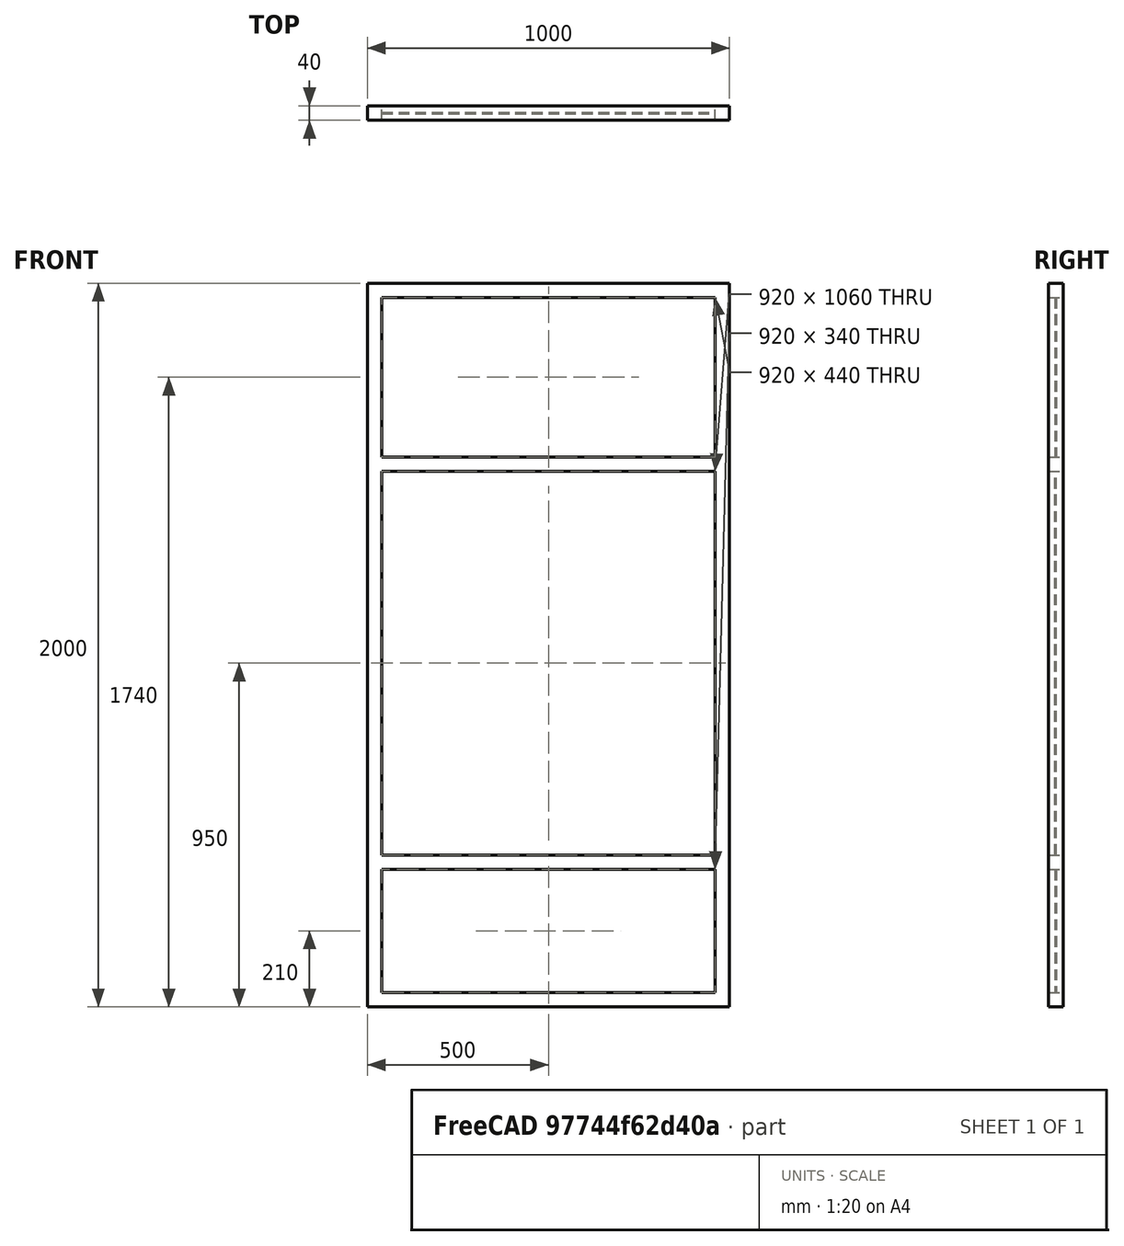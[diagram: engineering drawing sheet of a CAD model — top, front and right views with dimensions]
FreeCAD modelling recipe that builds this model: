
FCSTD DOCUMENT  (FreeCAD 0.16R6704 (Git))
Label: Window with 3 vertical fixed glass
License: CreativeCommons Attribution
LicenseURL: http://creativecommons.org/licenses/by/4.0/
objects: Sketcher::SketchObject×1, Part::FeaturePython×1
note: 2 computed .brp shape members not serialized (recipe doc carries the construction recipe); baked Part::Feature solids carry a one-line shape summary decoded from their .brp

FEATURE [Sketcher::SketchObject] Sketch114  label="Esboço caixilho fixo 3"
  Placement = pos=(0,0,0) rot=(1,0,0;1.5708rad)
  sketch-geometry (24):
    g0: LineSegment StartX=1000 StartY=2000 StartZ=0 EndX=0 EndY=2000 EndZ=0
    g1: LineSegment StartX=0 StartY=2000 StartZ=0 EndX=0 EndY=0 EndZ=0
    g2: LineSegment StartX=0 StartY=0 StartZ=0 EndX=1000 EndY=0 EndZ=0
    g3: LineSegment StartX=1000 StartY=0 StartZ=0 EndX=1000 EndY=2000 EndZ=0
    g4: LineSegment StartX=40 StartY=380 StartZ=0 EndX=960 EndY=380 EndZ=0
    g5: LineSegment StartX=960 StartY=380 StartZ=0 EndX=960 EndY=40 EndZ=0
    g6: LineSegment StartX=960 StartY=40 StartZ=0 EndX=40 EndY=40 EndZ=0
    g7: LineSegment StartX=40 StartY=40 StartZ=0 EndX=40 EndY=380 EndZ=0
    g8: LineSegment StartX=40 StartY=1960 StartZ=0 EndX=960 EndY=1960 EndZ=0
    g9: LineSegment StartX=960 StartY=1960 StartZ=0 EndX=960 EndY=1520 EndZ=0
    g10: LineSegment StartX=960 StartY=1520 StartZ=0 EndX=40 EndY=1520 EndZ=0
    g11: LineSegment StartX=40 StartY=1520 StartZ=0 EndX=40 EndY=1960 EndZ=0
    g12: LineSegment StartX=40 StartY=420 StartZ=0 EndX=960 EndY=420 EndZ=0
    g13: LineSegment StartX=960 StartY=420 StartZ=0 EndX=960 EndY=1480 EndZ=0
    g14: LineSegment StartX=960 StartY=1480 StartZ=0 EndX=40 EndY=1480 EndZ=0
    g15: LineSegment StartX=40 StartY=1480 StartZ=0 EndX=40 EndY=420 EndZ=0
    g16: LineSegment [constr] StartX=-293.148 StartY=1500 StartZ=0 EndX=1289.03 EndY=1500 EndZ=0
    g17: LineSegment [constr] StartX=-323.917 StartY=400 StartZ=0 EndX=1257.67 EndY=400 EndZ=0
    g18: LineSegment [constr] StartX=194.907 StartY=2000 StartZ=0 EndX=194.907 EndY=1960 EndZ=0
    g19: LineSegment [constr] StartX=328.544 StartY=1520 StartZ=0 EndX=328.544 EndY=1480 EndZ=0
    g20: LineSegment [constr] StartX=0 StartY=1579.86 StartZ=0 EndX=40 EndY=1579.86 EndZ=0
    g21: LineSegment [constr] StartX=960 StartY=1722.52 StartZ=0 EndX=1000 EndY=1722.52 EndZ=0
    g22: LineSegment [constr] StartX=601.933 StartY=420 StartZ=0 EndX=601.933 EndY=380 EndZ=0
    g23: LineSegment [constr] StartX=597.798 StartY=40 StartZ=0 EndX=597.798 EndY=0 EndZ=0
  constraints (67):
    c: Coincident(g0,g1)
    c: Horizontal(g0)
    c: Coincident(g1,g2)
    c: Vertical(g1)
    c: Coincident(g2,g3)
    c: Horizontal(g2)
    c: Coincident(g3,g0)
    c: Coincident(g4,g5)
    c: Horizontal(g4)
    c: Coincident(g5,g6)
    c: Vertical(g5)
    c: Coincident(g6,g7)
    c: Horizontal(g6)
    c: Coincident(g7,g4)
    c: Coincident(g8,g9)
    c: Horizontal(g8)
    c: Coincident(g9,g10)
    c: Vertical(g9)
    c: Coincident(g10,g11)
    c: Horizontal(g10)
    c: Coincident(g11,g8)
    c: Coincident(g12,g13)
    c: Horizontal(g12)
    c: Coincident(g13,g14)
    c: Vertical(g13)
    c: Coincident(g14,g15)
    c: Horizontal(g14)
    c: Coincident(g15,g12)
    c: DistanceX(g0,g8) = 40  'Montantes'
    c: DistanceX(g10,g14) = 0  'Constraint31'
    c: DistanceX(g9,g13) = 0
    c: DistanceX(g12,g4) = 0
    c: DistanceX(g12,g4) = 0
    c: DistanceX(g0,g0) = 1000  'Largura do vão'
    c: DistanceY(g2,g0) = 2000  'Altura do vão'
    c: Symmetric(g14,g10,g16)  'Constraint39'
    c: DistanceY(g16,g0) = 500  'Altura parte superior'
    c: DistanceY(g2,g17) = 400  'Altura parte inferior'
    c: Coincident(g1,g-1)  'Constraint42'
    c: Vertical(g11)  'Constraint40'
    c: Vertical(g7)
    c: Vertical(g3)
    c: Vertical(g15)
    c: Symmetric(g12,g4,g17)
    c: PointOnObject(g18,g0)
    c: PointOnObject(g18,g8)
    c: PointOnObject(g20,g1)
    c: PointOnObject(g20,g11)
    c: PointOnObject(g19,g10)
    c: PointOnObject(g19,g14)
    c: PointOnObject(g21,g9)
    c: PointOnObject(g21,g3)
    c: PointOnObject(g22,g12)
    c: PointOnObject(g22,g4)
    c: PointOnObject(g23,g6)
    c: PointOnObject(g23,g2)
    c: Equal(g18,g20)
    c: Equal(g20,g21)
    c: Equal(g21,g19)
    c: Equal(g19,g22)
    c: Equal(g22,g23)
    c: Angle(g18) = -1.5708
    c: Angle(g20) = 0
    c: Angle(g19) = -1.5708
    c: Angle(g21) = 0
    c: Angle(g22) = -1.5708
    c: Angle(g23) = -1.5708
FEATURE [Part::FeaturePython] Window082  label="Window with 3 vertical fixed glass"  # WARN: FeaturePython — macro-defined, semantics opaque (R4)
  Base = -> Sketch114
  Height = 0
  HoleDepth = 0
  MoveWithHost = true
  Normal = (0,1,0)
  Preset = 0
  Role = 0
  Width = 0
  WindowParts = MONTANTES | Frame | Wire0,Wire1,Wire2,Wire3 | 40.0 | 0.0 | VIDRO 1 | Glass panel | Wire2 | 4.0 | 18.0 | VIDRO 2 | Glass panel | Wire3 | 4.0 | 18.0 | VIDRO 3 | Glass panel | Wire1 | 4.0 | 18.0
